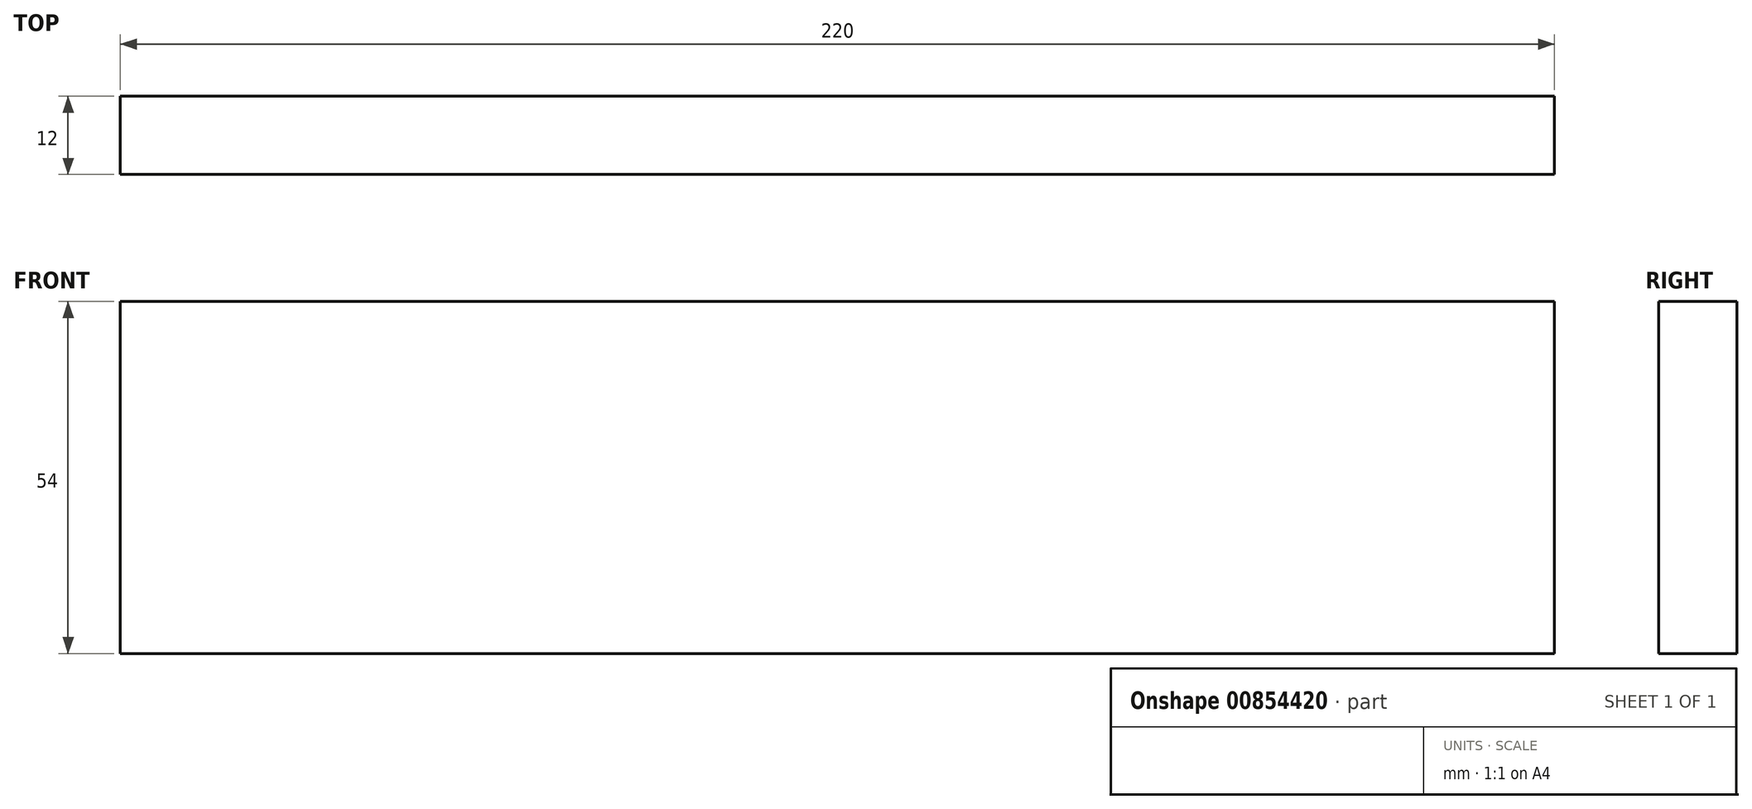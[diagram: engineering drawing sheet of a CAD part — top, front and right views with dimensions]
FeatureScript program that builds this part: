
annotation { "Feature Type Name" : "Feature", "Feature Type Description" : "" }
export const myFeature = defineFeature(function(context is Context, id is Id, definition is map)
    precondition{}
    {
        {
            var Q0;
            Q0=qCreatedBy(makeId("Front.planeOp"),FACE);
            var sketch = newSketch(context, id + "F0", { "sketchPlane" : qUnion([Q0])});
            skLineSegment(sketch, "E0.bottom", {"start": v(-110, 27) * mm, "end": v(110, 27) * mm});
            skLineSegment(sketch, "E0.top", {"start": v(-110, -27) * mm, "end": v(110, -27) * mm});
            skLineSegment(sketch, "E0.left", {"start": v(-110, 27) * mm, "end": v(-110, -27) * mm});
            skLineSegment(sketch, "E0.right", {"start": v(110, 27) * mm, "end": v(110, -27) * mm});
            skPoint(sketch, "E0.middle", {"position": v(0, 0) * mm});
            skSolve(sketch);
        }
        {
            var Q0;
            Q0 = qSketchRegion(id + "F0", true);
            extrude(context, id + "F1", {"entities" : qUnion([Q0]), "depth" : 12 * mm, "offsetDistance" : 25.4 * mm});
        }
    });
